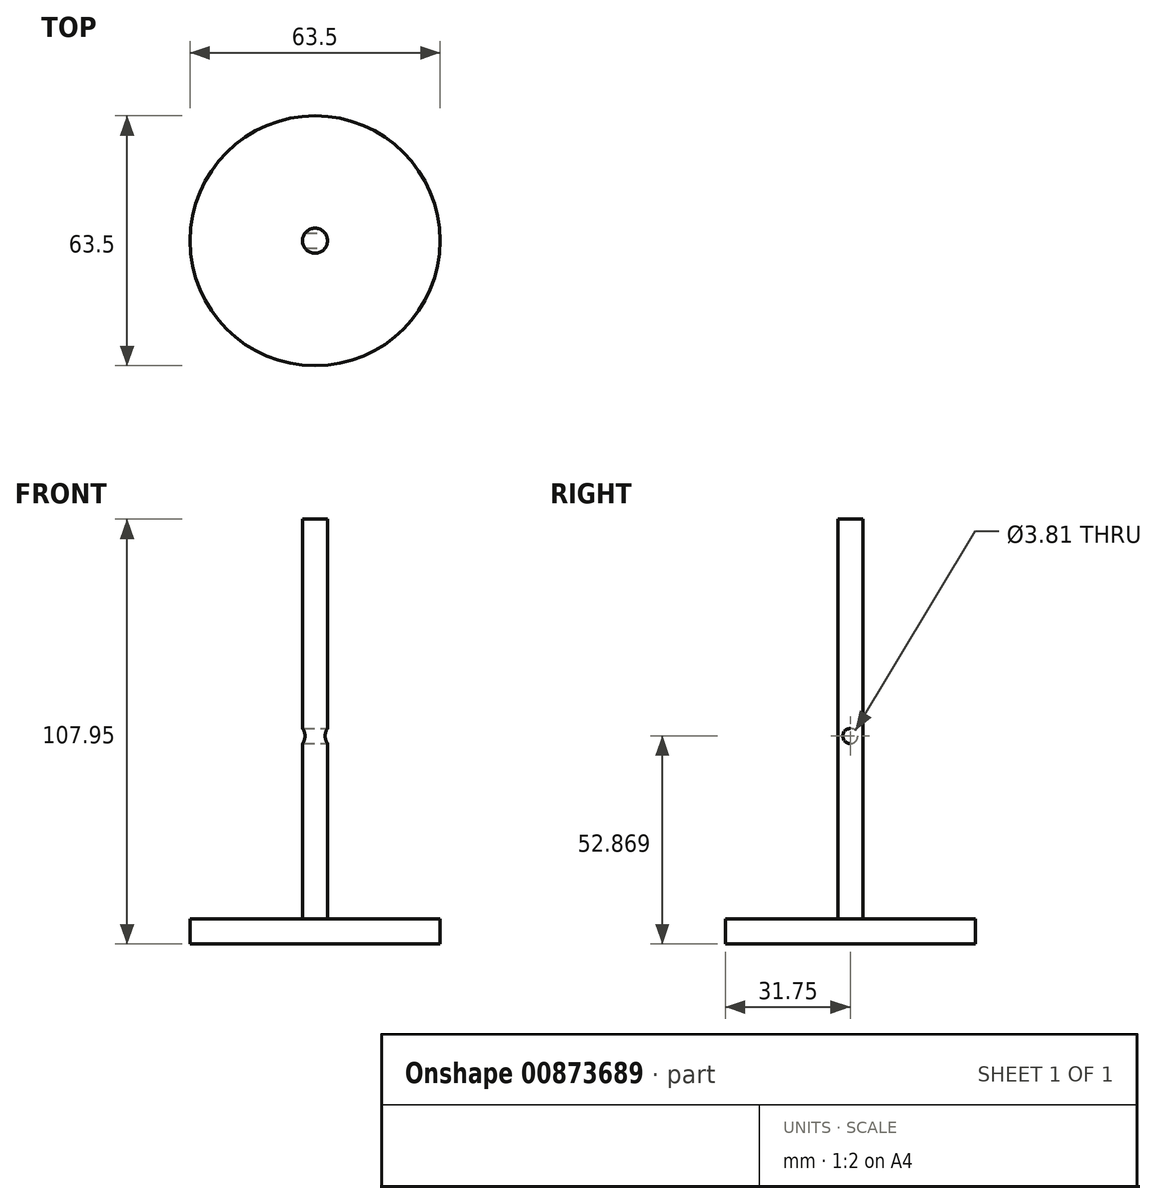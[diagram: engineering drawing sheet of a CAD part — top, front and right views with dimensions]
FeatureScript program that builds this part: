
annotation { "Feature Type Name" : "Feature", "Feature Type Description" : "" }
export const myFeature = defineFeature(function(context is Context, id is Id, definition is map)
    precondition{}
    {
        {
            var Q0;
            Q0=qCreatedBy(makeId("Top.planeOp"),FACE);
            var sketch = newSketch(context, id + "F0", { "sketchPlane" : qUnion([Q0])});
            skCircle(sketch, "E0", {"center": v(0, 0) * mm, "radius": 31.75 * mm});
            skSolve(sketch);
        }
        {
            var Q0;
            Q0 = qSketchRegion(id + "F0", true);
            extrude(context, id + "F1", {"entities" : qUnion([Q0]), "depth" : 6.35 * mm, "offsetDistance" : 25.4 * mm});
        }
        {
            var Q0;
            Q0=makeQuery(id+"F1.opExtrude","CAP_FACE",FACE,{"disambiguationData":[OSD([sQuery(id+"F0.wireOp",EDGE,"E0")])],"isStart":false});
            var sketch = newSketch(context, id + "F2", { "sketchPlane" : qUnion([Q0])});
            skCircle(sketch, "E1", {"center": v(0, 0) * mm, "radius": 3.18 * mm});
            skSolve(sketch);
        }
        {
            var Q0;
            Q0 = qSketchRegion(id + "F2", true);
            extrude(context, id + "F3", {"entities" : qUnion([Q0]), "operationType" : NewBodyOperationType.ADD, "depth" : 101.6 * mm, "offsetDistance" : 25.4 * mm});
        }
        {
            var Q0;
            Q0=qCreatedBy(makeId("Right.planeOp"),FACE);
            var sketch = newSketch(context, id + "F4", { "sketchPlane" : qUnion([Q0])});
            skCircle(sketch, "E2", {"center": v(0, 52.87) * mm, "radius": 1.9 * mm});
            skSolve(sketch);
        }
        {
            var Q0;
            Q0 = qSketchRegion(id + "F4", true);
            extrude(context, id + "F5", {"entities" : qUnion([Q0]), "operationType" : NewBodyOperationType.REMOVE, "endBound" : BoundingType.SYMMETRIC, "oppositeDirection" : true, "depth" : 25.4 * mm, "offsetDistance" : 25.4 * mm});
        }
    });
